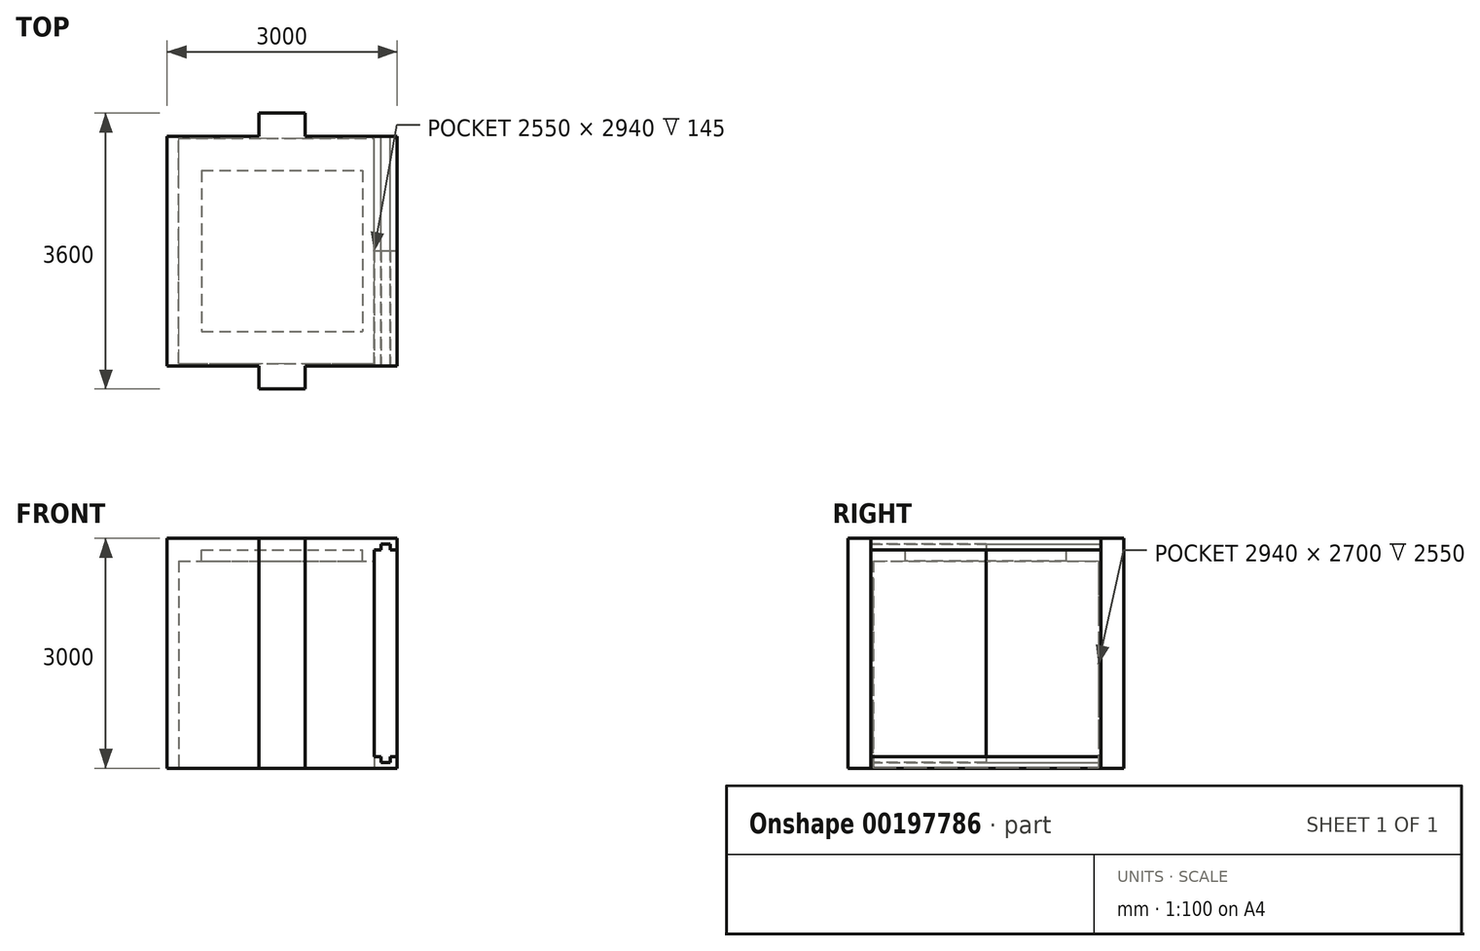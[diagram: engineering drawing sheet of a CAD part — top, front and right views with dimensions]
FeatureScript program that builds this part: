
annotation { "Feature Type Name" : "Feature", "Feature Type Description" : "" }
export const myFeature = defineFeature(function(context is Context, id is Id, definition is map)
    precondition{}
    {
        {
            var Q0;
            Q0=qCreatedBy(makeId("Top.planeOp"),FACE);
            var sketch = newSketch(context, id + "F0", { "sketchPlane" : qUnion([Q0])});
            skLineSegment(sketch, "E0.bottom", {"start": v(-1500, 1500) * mm, "end": v(1200, 1500) * mm});
            skLineSegment(sketch, "E0.top", {"start": v(-1500, -1500) * mm, "end": v(1200, -1500) * mm});
            skLineSegment(sketch, "E0.left", {"start": v(-1500, 1500) * mm, "end": v(-1500, -1500) * mm});
            skPoint(sketch, "E0.middle", {"position": v(0, 0) * mm});
            skLineSegment(sketch, "E1", {"start": v(-300, 1500) * mm, "end": v(-300, 1800) * mm});
            skLineSegment(sketch, "E2", {"start": v(-300, 1800) * mm, "end": v(300, 1800) * mm});
            skLineSegment(sketch, "E3", {"start": v(300, 1800) * mm, "end": v(300, 1500) * mm});
            skLineSegment(sketch, "E4.MirrorCS", {"start": v(-300, -1500) * mm, "end": v(-300, -1800) * mm});
            skLineSegment(sketch, "E5.MirrorCS", {"start": v(-300, -1800) * mm, "end": v(300, -1800) * mm});
            skLineSegment(sketch, "E6.MirrorCS", {"start": v(300, -1800) * mm, "end": v(300, -1500) * mm});
            skLineSegment(sketch, "E7", {"start": v(1200, 1500) * mm, "end": v(1200, -1500) * mm});
            skPoint(sketch, "E8.start.orphan", {"position": v(1200, 0) * mm});
            skSolve(sketch);
        }
        {
            var Q0;
            Q0 = qSketchRegion(id + "F0", true);
            extrude(context, id + "F1", {"entities" : qUnion([Q0]), "depth" : 3000 * mm});
        }
        {
            var Q0;
            Q0=makeQuery(id+"F1.opExtrude","CAP_FACE",FACE,{"disambiguationData":[OSD([sQuery(id+"F0.wireOp",EDGE,"E0.bottom"),sQuery(id+"F0.wireOp",EDGE,"E0.top"),sQuery(id+"F0.wireOp",EDGE,"E0.left"),sQuery(id+"F0.wireOp",EDGE,"E0.right"),sQuery(id+"F0.wireOp",EDGE,"E1"),sQuery(id+"F0.wireOp",EDGE,"E2"),sQuery(id+"F0.wireOp",EDGE,"E3"),sQuery(id+"F0.wireOp",EDGE,"E4.MirrorCS"),sQuery(id+"F0.wireOp",EDGE,"E5.MirrorCS"),sQuery(id+"F0.wireOp",EDGE,"E6.MirrorCS")])],"isStart":false});
            var sketch = newSketch(context, id + "F2", { "sketchPlane" : qUnion([Q0])});
            skLineSegment(sketch, "E9.bottom", {"start": v(-1050, 1050) * mm, "end": v(1050, 1050) * mm});
            skLineSegment(sketch, "E9.top", {"start": v(-1050, -1050) * mm, "end": v(1050, -1050) * mm});
            skLineSegment(sketch, "E9.left", {"start": v(-1050, 1050) * mm, "end": v(-1050, -1050) * mm});
            skLineSegment(sketch, "E9.right", {"start": v(1050, 1050) * mm, "end": v(1050, -1050) * mm});
            skPoint(sketch, "E9.middle", {"position": v(0, 0) * mm});
            skSolve(sketch);
        }
        {
            var Q0;
            Q0 = qSketchRegion(id + "F2", true);
            extrude(context, id + "F3", {"entities" : qUnion([Q0]), "operationType" : NewBodyOperationType.REMOVE, "oppositeDirection" : true, "depth" : 3000 * mm});
        }
        {
            var Q0;
            Q0=qCreatedBy(makeId("Top.planeOp"),FACE);
            var sketch = newSketch(context, id + "F4", { "sketchPlane" : qUnion([Q0])});
            skLineSegment(sketch, "E10.bottom", {"start": v(-1050, 1050) * mm, "end": v(1050, 1050) * mm});
            skLineSegment(sketch, "E10.top", {"start": v(-1050, -1050) * mm, "end": v(1050, -1050) * mm});
            skLineSegment(sketch, "E10.left", {"start": v(-1050, 1050) * mm, "end": v(-1050, -1050) * mm});
            skLineSegment(sketch, "E10.right", {"start": v(1050, 1050) * mm, "end": v(1050, -1050) * mm});
            skPoint(sketch, "E10.middle", {"position": v(0, 0) * mm});
            skSolve(sketch);
        }
        {
            var Q0;
            Q0 = qSketchRegion(id + "F4", true);
            extrude(context, id + "F5", {"entities" : qUnion([Q0]), "operationType" : NewBodyOperationType.ADD, "depth" : 150 * mm});
        }
        {
            var Q0;
            Q0=makeQuery(id+"F1.opExtrude","CAP_FACE",FACE,{"disambiguationData":[OSD([sQuery(id+"F0.wireOp",EDGE,"E0.bottom"),sQuery(id+"F0.wireOp",EDGE,"E0.top"),sQuery(id+"F0.wireOp",EDGE,"E0.left"),sQuery(id+"F0.wireOp",EDGE,"E0.right"),sQuery(id+"F0.wireOp",EDGE,"E1"),sQuery(id+"F0.wireOp",EDGE,"E2"),sQuery(id+"F0.wireOp",EDGE,"E3"),sQuery(id+"F0.wireOp",EDGE,"E4.MirrorCS"),sQuery(id+"F0.wireOp",EDGE,"E5.MirrorCS"),sQuery(id+"F0.wireOp",EDGE,"E6.MirrorCS")])],"isStart":false});
            var sketch = newSketch(context, id + "F6", { "sketchPlane" : qUnion([Q0])});
            skLineSegment(sketch, "E11.bottom", {"start": v(-1050, 1050) * mm, "end": v(1050, 1050) * mm});
            skLineSegment(sketch, "E11.top", {"start": v(-1050, -1050) * mm, "end": v(1050, -1050) * mm});
            skLineSegment(sketch, "E11.left", {"start": v(-1050, 1050) * mm, "end": v(-1050, -1050) * mm});
            skLineSegment(sketch, "E11.right", {"start": v(1050, 1050) * mm, "end": v(1050, -1050) * mm});
            skPoint(sketch, "E11.middle", {"position": v(0, 0) * mm});
            skSolve(sketch);
        }
        {
            var Q0;
            Q0 = qSketchRegion(id + "F6", true);
            extrude(context, id + "F7", {"entities" : qUnion([Q0]), "operationType" : NewBodyOperationType.ADD, "oppositeDirection" : true, "depth" : 150 * mm});
        }
        {
            var Q0;
            {var subQ0=sQuery(id+"F0.wireOp",EDGE,"E0.bottom");Q0=makeQuery(id+"F1.opExtrude","SWEPT_FACE",FACE,{"disambiguationData":[OSD([subQ0]),TDD([makeQuery(id+"F0.imprint","IMPRINT",EDGE,{"disambiguationData":[TD([[makeQuery(id+"F0.imprint","INTERSECT",VERTEX,{"derivedFrom":[subQ0,sQuery(id+"F0.wireOp",EDGE,"E7")]}),1.0]])],"derivedFrom":subQ0})])]});}
            var sketch = newSketch(context, id + "F8", { "sketchPlane" : qUnion([Q0])});
            skLineSegment(sketch, "E12", {"start": v(-1200, 3000) * mm, "end": v(-1500, 3000) * mm});
            skLineSegment(sketch, "E13", {"start": v(-1500, 3000) * mm, "end": v(-1500, 2850) * mm});
            skLineSegment(sketch, "E14", {"start": v(-1500, 2850) * mm, "end": v(-1410, 2850) * mm});
            skLineSegment(sketch, "E15", {"start": v(-1410, 2850) * mm, "end": v(-1410, 2925) * mm});
            skLineSegment(sketch, "E16", {"start": v(-1410, 2925) * mm, "end": v(-1290, 2925) * mm});
            skLineSegment(sketch, "E17", {"start": v(-1290, 2925) * mm, "end": v(-1290, 2850) * mm});
            skLineSegment(sketch, "E18", {"start": v(-1290, 2850) * mm, "end": v(-1200, 2850) * mm});
            skLineSegment(sketch, "E19", {"start": v(-1200, 3000) * mm, "end": v(-1200, 2850) * mm});
            skSolve(sketch);
        }
        {
            var Q0;
            Q0 = qSketchRegion(id + "F8", true);
            extrude(context, id + "F9", {"entities" : qUnion([Q0]), "operationType" : NewBodyOperationType.ADD, "oppositeDirection" : true, "depth" : 3000 * mm});
        }
        {
            var Q0;
            Q0=makeQuery(id+"F1.opExtrude","SWEPT_FACE",FACE,{"disambiguationData":[OSD([sQuery(id+"F0.wireOp",EDGE,"E7")])]});
            var sketch = newSketch(context, id + "F10", { "sketchPlane" : qUnion([Q0])});
            skLineSegment(sketch, "E20.bottom", {"start": v(-1470, 2705) * mm, "end": v(1470, 2705) * mm});
            skLineSegment(sketch, "E20.top", {"start": v(-1470, 5) * mm, "end": v(1470, 5) * mm});
            skLineSegment(sketch, "E20.left", {"start": v(-1470, 2705) * mm, "end": v(-1470, 5) * mm});
            skLineSegment(sketch, "E20.right", {"start": v(1470, 2705) * mm, "end": v(1470, 5) * mm});
            skPoint(sketch, "E20.middle", {"position": v(0, 1355) * mm});
            skSolve(sketch);
        }
        {
            var Q0;
            Q0 = qSketchRegion(id + "F10", true);
            extrude(context, id + "F11", {"entities" : qUnion([Q0]), "operationType" : NewBodyOperationType.REMOVE, "oppositeDirection" : true, "depth" : 2550 * mm});
        }
        {
            var Q0;
            {var subQ0=sQuery(id+"F0.wireOp",EDGE,"E0.bottom");Q0=makeQuery(id+"F9.boolean.opBoolean","MERGE",FACE,{"derivedFrom":[makeQuery(id+"F1.opExtrude","SWEPT_FACE",FACE,{"disambiguationData":[OSD([subQ0]),TDD([makeQuery(id+"F0.imprint","IMPRINT",EDGE,{"disambiguationData":[TD([[makeQuery(id+"F0.imprint","INTERSECT",VERTEX,{"derivedFrom":[subQ0,sQuery(id+"F0.wireOp",EDGE,"E7")]}),1.0]])],"derivedFrom":subQ0})])]}),makeQuery(id+"F9.opExtrude","CAP_FACE",FACE,{"disambiguationData":[OSD([sQuery(id+"F8.wireOp",EDGE,"E12"),sQuery(id+"F8.wireOp",EDGE,"E13"),sQuery(id+"F8.wireOp",EDGE,"E14"),sQuery(id+"F8.wireOp",EDGE,"E15"),sQuery(id+"F8.wireOp",EDGE,"E16"),sQuery(id+"F8.wireOp",EDGE,"E17"),sQuery(id+"F8.wireOp",EDGE,"E18"),sQuery(id+"F8.wireOp",EDGE,"E19")])],"isStart":true})]});}
            var sketch = newSketch(context, id + "F12", { "sketchPlane" : qUnion([Q0])});
            skLineSegment(sketch, "E21", {"start": v(-1200, 0) * mm, "end": v(-1500, 0) * mm});
            skLineSegment(sketch, "E22", {"start": v(-1500, 0) * mm, "end": v(-1500, 150) * mm});
            skLineSegment(sketch, "E23", {"start": v(-1500, 150) * mm, "end": v(-1410, 150) * mm});
            skLineSegment(sketch, "E24", {"start": v(-1410, 150) * mm, "end": v(-1410, 75) * mm});
            skLineSegment(sketch, "E25", {"start": v(-1410, 75) * mm, "end": v(-1290, 75) * mm});
            skLineSegment(sketch, "E26", {"start": v(-1290, 75) * mm, "end": v(-1290, 150) * mm});
            skLineSegment(sketch, "E27", {"start": v(-1290, 150) * mm, "end": v(-1200, 150) * mm});
            skLineSegment(sketch, "E28", {"start": v(-1200, 150) * mm, "end": v(-1200, 0) * mm});
            skSolve(sketch);
        }
        {
            var Q0;
            Q0 = qSketchRegion(id + "F12", true);
            extrude(context, id + "F13", {"entities" : qUnion([Q0]), "operationType" : NewBodyOperationType.ADD, "oppositeDirection" : true, "depth" : 3000 * mm});
        }
        {
            var Q0;
            {var subQ0=sQuery(id+"F0.wireOp",EDGE,"E0.bottom");Q0=makeQuery(id+"F13.boolean.opBoolean","MERGE",FACE,{"derivedFrom":[makeQuery(id+"F9.boolean.opBoolean","MERGE",FACE,{"derivedFrom":[makeQuery(id+"F1.opExtrude","SWEPT_FACE",FACE,{"disambiguationData":[OSD([subQ0]),TDD([makeQuery(id+"F0.imprint","IMPRINT",EDGE,{"disambiguationData":[TD([[makeQuery(id+"F0.imprint","INTERSECT",VERTEX,{"derivedFrom":[subQ0,sQuery(id+"F0.wireOp",EDGE,"E7")]}),1.0]])],"derivedFrom":subQ0})])]}),makeQuery(id+"F9.opExtrude","CAP_FACE",FACE,{"disambiguationData":[OSD([sQuery(id+"F8.wireOp",EDGE,"E12"),sQuery(id+"F8.wireOp",EDGE,"E13"),sQuery(id+"F8.wireOp",EDGE,"E14"),sQuery(id+"F8.wireOp",EDGE,"E15"),sQuery(id+"F8.wireOp",EDGE,"E16"),sQuery(id+"F8.wireOp",EDGE,"E17"),sQuery(id+"F8.wireOp",EDGE,"E18"),sQuery(id+"F8.wireOp",EDGE,"E19")])],"isStart":true})]}),makeQuery(id+"F13.opExtrude","CAP_FACE",FACE,{"disambiguationData":[OSD([sQuery(id+"F12.wireOp",EDGE,"hug7QCPa-GxZ1-TSAt-IC7Z-w67bIKYh1you"),sQuery(id+"F12.wireOp",EDGE,"zlwaCWf6-FMFH-thxJ-zFcJ-GuFhcXhvfoc0"),sQuery(id+"F12.wireOp",EDGE,"0EdmMTyD-5i8C-5uJw-xAQZ-3ZzquauYSfZ3"),sQuery(id+"F12.wireOp",EDGE,"G8kcmfBX-Ja0w-3OlD-Dxyx-30gYmuTs85ml"),sQuery(id+"F12.wireOp",EDGE,"5mWS4ZSk-yXnk-gHQj-xdkv-r3xuj4l9kbUt"),sQuery(id+"F12.wireOp",EDGE,"H64zZp5d-78BU-SMuF-AOEI-HPVCNYyMH6M1"),sQuery(id+"F12.wireOp",EDGE,"DWSHwkkV-hsRF-nHit-ZVEL-xkg39FNqW3zN"),sQuery(id+"F12.wireOp",EDGE,"0eAQGVw0-3wB6-UMqD-h2DD-D08MPByl0bGS")])],"isStart":true})]});}
            var sketch = newSketch(context, id + "F14", { "sketchPlane" : qUnion([Q0])});
            skLineSegment(sketch, "E29", {"start": v(-1500, 2850) * mm, "end": v(-1410, 2850) * mm});
            skLineSegment(sketch, "E30", {"start": v(-1410, 2850) * mm, "end": v(-1410, 2925) * mm});
            skLineSegment(sketch, "E31", {"start": v(-1410, 2925) * mm, "end": v(-1290, 2925) * mm});
            skLineSegment(sketch, "E32", {"start": v(-1290, 2925) * mm, "end": v(-1290, 2850) * mm});
            skLineSegment(sketch, "E33", {"start": v(-1290, 2850) * mm, "end": v(-1200, 2850) * mm});
            skLineSegment(sketch, "E34", {"start": v(-1200, 2850) * mm, "end": v(-1200, 150) * mm});
            skLineSegment(sketch, "E35", {"start": v(-1200, 150) * mm, "end": v(-1290, 150) * mm});
            skLineSegment(sketch, "E36", {"start": v(-1290, 150) * mm, "end": v(-1290, 75) * mm});
            skLineSegment(sketch, "E37", {"start": v(-1290, 75) * mm, "end": v(-1410, 75) * mm});
            skLineSegment(sketch, "E38", {"start": v(-1410, 75) * mm, "end": v(-1410, 150) * mm});
            skLineSegment(sketch, "E39", {"start": v(-1410, 150) * mm, "end": v(-1500, 150) * mm});
            skLineSegment(sketch, "E40", {"start": v(-1500, 150) * mm, "end": v(-1500, 2850) * mm});
            skSolve(sketch);
        }
        {
            var Q0;
            Q0 = qSketchRegion(id + "F14", true);
            extrude(context, id + "F15", {"entities" : qUnion([Q0]), "oppositeDirection" : true, "depth" : 1500 * mm});
        }
        {
            var Q0;
            {var subQ0=sQuery(id+"F0.wireOp",EDGE,"E0.top");Q0=makeQuery(id+"F13.boolean.opBoolean","MERGE",FACE,{"derivedFrom":[makeQuery(id+"F9.boolean.opBoolean","MERGE",FACE,{"derivedFrom":[makeQuery(id+"F1.opExtrude","SWEPT_FACE",FACE,{"disambiguationData":[OSD([subQ0]),TDD([makeQuery(id+"F0.imprint","IMPRINT",EDGE,{"disambiguationData":[TD([[makeQuery(id+"F0.imprint","INTERSECT",VERTEX,{"derivedFrom":[subQ0,sQuery(id+"F0.wireOp",EDGE,"E7")]}),1.0]])],"derivedFrom":subQ0})])]}),makeQuery(id+"F9.opExtrude","CAP_FACE",FACE,{"disambiguationData":[OSD([sQuery(id+"F8.wireOp",EDGE,"E12"),sQuery(id+"F8.wireOp",EDGE,"E13"),sQuery(id+"F8.wireOp",EDGE,"E14"),sQuery(id+"F8.wireOp",EDGE,"E15"),sQuery(id+"F8.wireOp",EDGE,"E16"),sQuery(id+"F8.wireOp",EDGE,"E17"),sQuery(id+"F8.wireOp",EDGE,"E18"),sQuery(id+"F8.wireOp",EDGE,"E19")])],"isStart":false})]}),makeQuery(id+"F13.opExtrude","CAP_FACE",FACE,{"disambiguationData":[OSD([sQuery(id+"F12.wireOp",EDGE,"hug7QCPa-GxZ1-TSAt-IC7Z-w67bIKYh1you"),sQuery(id+"F12.wireOp",EDGE,"zlwaCWf6-FMFH-thxJ-zFcJ-GuFhcXhvfoc0"),sQuery(id+"F12.wireOp",EDGE,"0EdmMTyD-5i8C-5uJw-xAQZ-3ZzquauYSfZ3"),sQuery(id+"F12.wireOp",EDGE,"G8kcmfBX-Ja0w-3OlD-Dxyx-30gYmuTs85ml"),sQuery(id+"F12.wireOp",EDGE,"5mWS4ZSk-yXnk-gHQj-xdkv-r3xuj4l9kbUt"),sQuery(id+"F12.wireOp",EDGE,"H64zZp5d-78BU-SMuF-AOEI-HPVCNYyMH6M1"),sQuery(id+"F12.wireOp",EDGE,"DWSHwkkV-hsRF-nHit-ZVEL-xkg39FNqW3zN"),sQuery(id+"F12.wireOp",EDGE,"0eAQGVw0-3wB6-UMqD-h2DD-D08MPByl0bGS")])],"isStart":false})]});}
            var sketch = newSketch(context, id + "F16", { "sketchPlane" : qUnion([Q0])});
            skLineSegment(sketch, "E41", {"start": v(1200, 2850) * mm, "end": v(1290, 2850) * mm});
            skLineSegment(sketch, "E42", {"start": v(1290, 2850) * mm, "end": v(1290, 2925) * mm});
            skLineSegment(sketch, "E43", {"start": v(1290, 2925) * mm, "end": v(1410, 2925) * mm});
            skLineSegment(sketch, "E44", {"start": v(1410, 2925) * mm, "end": v(1410, 2850) * mm});
            skLineSegment(sketch, "E45", {"start": v(1410, 2850) * mm, "end": v(1500, 2850) * mm});
            skLineSegment(sketch, "E46", {"start": v(1500, 2850) * mm, "end": v(1500, 150) * mm});
            skLineSegment(sketch, "E47", {"start": v(1500, 150) * mm, "end": v(1410, 150) * mm});
            skLineSegment(sketch, "E48", {"start": v(1410, 150) * mm, "end": v(1410, 75) * mm});
            skLineSegment(sketch, "E49", {"start": v(1410, 75) * mm, "end": v(1290, 75) * mm});
            skLineSegment(sketch, "E50", {"start": v(1290, 75) * mm, "end": v(1290, 150) * mm});
            skLineSegment(sketch, "E51", {"start": v(1290, 150) * mm, "end": v(1200, 150) * mm});
            skLineSegment(sketch, "E52", {"start": v(1200, 150) * mm, "end": v(1200, 2850) * mm});
            skSolve(sketch);
        }
        {
            var Q0;
            Q0 = qSketchRegion(id + "F16", true);
            extrude(context, id + "F17", {"entities" : qUnion([Q0]), "oppositeDirection" : true, "depth" : 1500 * mm});
        }
    });
